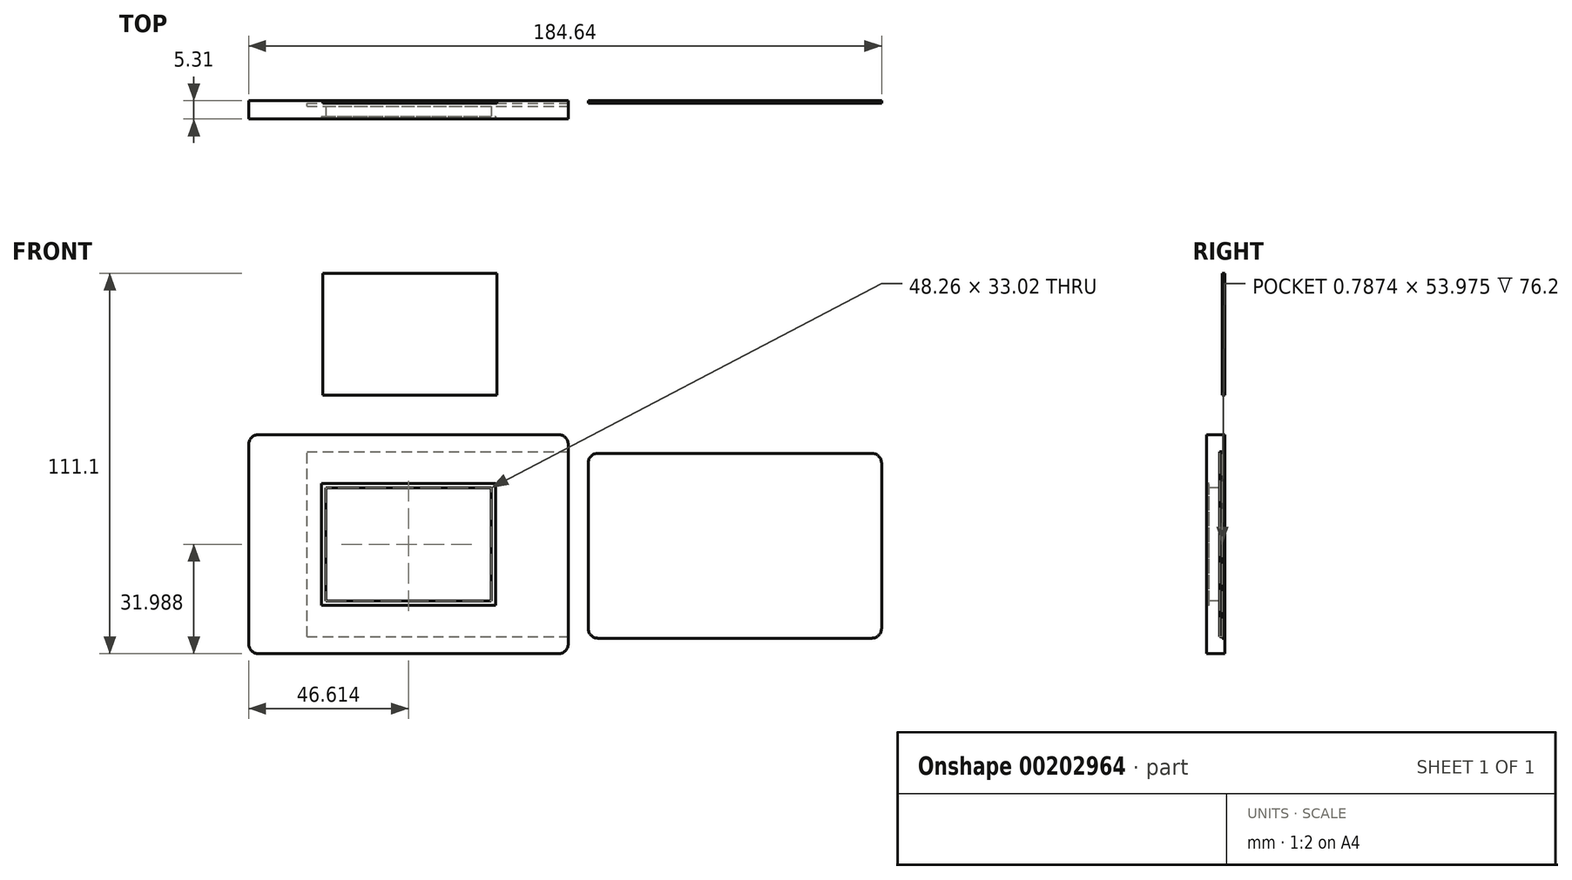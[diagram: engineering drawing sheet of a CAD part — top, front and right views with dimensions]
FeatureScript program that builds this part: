
annotation { "Feature Type Name" : "Feature", "Feature Type Description" : "" }
export const myFeature = defineFeature(function(context is Context, id is Id, definition is map)
    precondition{}
    {
        {
            var Q0;
            Q0=qCreatedBy(makeId("Front.planeOp"),FACE);
            var sketch = newSketch(context, id + "F0", { "sketchPlane" : qUnion([Q0])});
            skLineSegment(sketch, "E0", {"start": v(0, -2.88) * mm, "end": v(0, -51.1) * mm});
            skLineSegment(sketch, "E1", {"start": v(2.88, -53.97) * mm, "end": v(82.72, -53.97) * mm});
            skLineSegment(sketch, "E2", {"start": v(85.6, -51.1) * mm, "end": v(85.6, -2.88) * mm});
            skLineSegment(sketch, "E3", {"start": v(82.72, 0) * mm, "end": v(2.88, 0) * mm});
            skPoint(sketch, "E4.visualSharp", {"position": v(0, 0) * mm});
            skArc(sketch, "E4.filletArc", {"start": v(2.88, 0) * mm, "mid": v(0.84, -0.84) * mm, "end": v(0, -2.88) * mm});
            skPoint(sketch, "E5.visualSharp", {"position": v(85.6, 0) * mm});
            skArc(sketch, "E5.filletArc", {"start": v(85.6, -2.88) * mm, "mid": v(84.75, -0.84) * mm, "end": v(82.72, 0) * mm});
            skPoint(sketch, "E6.visualSharp", {"position": v(85.6, -53.97) * mm});
            skArc(sketch, "E6.filletArc", {"start": v(82.72, -53.98) * mm, "mid": v(84.75, -53.13) * mm, "end": v(85.6, -51.1) * mm});
            skPoint(sketch, "E7.visualSharp", {"position": v(0, -53.97) * mm});
            skArc(sketch, "E7.filletArc", {"start": v(0, -51.1) * mm, "mid": v(0.84, -53.13) * mm, "end": v(2.88, -53.98) * mm});
            skLineSegment(sketch, "E8", {"start": v(-99.04, 2.58) * mm, "end": v(-99.04, -55.64) * mm});
            skLineSegment(sketch, "E9", {"start": v(-96.16, -58.52) * mm, "end": v(-8.7, -58.52) * mm});
            skLineSegment(sketch, "E10", {"start": v(-5.82, -55.64) * mm, "end": v(-5.82, 2.58) * mm});
            skLineSegment(sketch, "E11", {"start": v(-8.7, 5.46) * mm, "end": v(-96.16, 5.46) * mm});
            skPoint(sketch, "E12.visualSharp", {"position": v(-99.04, 5.46) * mm});
            skArc(sketch, "E12.filletArc", {"start": v(-96.16, 5.46) * mm, "mid": v(-98.2, 4.61) * mm, "end": v(-99.04, 2.58) * mm});
            skPoint(sketch, "E13.visualSharp", {"position": v(-5.82, 5.46) * mm});
            skArc(sketch, "E13.filletArc", {"start": v(-5.82, 2.58) * mm, "mid": v(-6.66, 4.61) * mm, "end": v(-8.7, 5.46) * mm});
            skPoint(sketch, "E14.visualSharp", {"position": v(-5.82, -58.52) * mm});
            skArc(sketch, "E14.filletArc", {"start": v(-8.7, -58.52) * mm, "mid": v(-6.66, -57.68) * mm, "end": v(-5.82, -55.64) * mm});
            skPoint(sketch, "E15.visualSharp", {"position": v(-99.04, -58.52) * mm});
            skArc(sketch, "E15.filletArc", {"start": v(-99.04, -55.64) * mm, "mid": v(-98.2, -57.68) * mm, "end": v(-96.16, -58.52) * mm});
            skSolve(sketch);
        }
        {
            var Q0;
            Q0=makeQuery(id+"F0.imprint","IMPRINT",FACE,{"disambiguationData":[TD([[makeQuery(id+"F0.imprint","IMPRINT",EDGE,{"derivedFrom":sQuery(id+"F0.wireOp",EDGE,"E0")}),1.0]])]});
            extrude(context, id + "F1", {"entities" : qUnion([Q0]), "depth" : 0.76 * mm});
        }
        {
            var Q0;
            Q0=makeQuery(id+"F0.imprint","IMPRINT",FACE,{"disambiguationData":[TD([[makeQuery(id+"F0.imprint","IMPRINT",EDGE,{"derivedFrom":sQuery(id+"F0.wireOp",EDGE,"E8")}),1.0]])]});
            extrude(context, id + "F2", {"entities" : qUnion([Q0]), "depth" : 5.3 * mm});
        }
        {
            var Q0;
            Q0=makeQuery(id+"F2.opExtrude","SWEPT_FACE",FACE,{"disambiguationData":[OSD([sQuery(id+"F0.wireOp",EDGE,"E10")])]});
            var sketch = newSketch(context, id + "F3", { "sketchPlane" : qUnion([Q0])});
            skLineSegment(sketch, "E16", {"start": v(0, -26.53) * mm, "end": v(-0.76, -26.53) * mm});
            skPoint(sketch, "E16.endSnap0", {"position": v(0, -26.53) * mm});
            skLineSegment(sketch, "E17", {"start": v(-1.55, -26.53) * mm, "end": v(-1.55, 0.46) * mm});
            skLineSegment(sketch, "E18", {"start": v(-1.55, -26.53) * mm, "end": v(-1.55, -53.52) * mm});
            skLineSegment(sketch, "E19", {"start": v(-0.76, -26.53) * mm, "end": v(-0.76, -53.52) * mm});
            skLineSegment(sketch, "E20", {"start": v(-0.76, -26.53) * mm, "end": v(-0.76, 0.46) * mm});
            skLineSegment(sketch, "E21", {"start": v(-1.55, 0.46) * mm, "end": v(-0.76, 0.46) * mm});
            skLineSegment(sketch, "E22", {"start": v(-1.55, -53.52) * mm, "end": v(-0.76, -53.52) * mm});
            skLineSegment(sketch, "E23", {"start": v(-0.76, -26.53) * mm, "end": v(-1.55, -26.53) * mm});
            skSolve(sketch);
        }
        {
            var Q0;
            Q0=makeQuery(id+"F2.opExtrude","CAP_FACE",FACE,{"disambiguationData":[OSD([sQuery(id+"F0.wireOp",EDGE,"E8"),sQuery(id+"F0.wireOp",EDGE,"E9"),sQuery(id+"F0.wireOp",EDGE,"E10"),sQuery(id+"F0.wireOp",EDGE,"E11"),sQuery(id+"F0.wireOp",EDGE,"E12.filletArc"),sQuery(id+"F0.wireOp",EDGE,"E13.filletArc"),sQuery(id+"F0.wireOp",EDGE,"E14.filletArc"),sQuery(id+"F0.wireOp",EDGE,"E15.filletArc")])],"isStart":false});
            var sketch = newSketch(context, id + "F4", { "sketchPlane" : qUnion([Q0])});
            skPoint(sketch, "E24.orphan", {"position": v(-5.82, -26.53) * mm});
            skPoint(sketch, "E25.orphan", {"position": v(-99.04, -26.53) * mm});
            skPoint(sketch, "E26.orphan", {"position": v(-52.43, -58.52) * mm});
            skPoint(sketch, "E27.orphan", {"position": v(-52.43, 5.46) * mm});
            skPoint(sketch, "E28", {"position": v(-52.43, -26.53) * mm});
            skLineSegment(sketch, "E29", {"start": v(-52.43, -26.53) * mm, "end": v(-52.43, -8.75) * mm});
            skLineSegment(sketch, "E30", {"start": v(-52.43, -26.53) * mm, "end": v(-52.43, -44.31) * mm});
            skLineSegment(sketch, "E31", {"start": v(-52.43, -26.53) * mm, "end": v(-77.83, -26.53) * mm});
            skLineSegment(sketch, "E32", {"start": v(-52.43, -26.53) * mm, "end": v(-27.03, -26.53) * mm});
            skLineSegment(sketch, "E33", {"start": v(-77.83, -26.53) * mm, "end": v(-77.83, -8.75) * mm});
            skLineSegment(sketch, "E34", {"start": v(-52.43, -8.75) * mm, "end": v(-77.83, -8.75) * mm});
            skLineSegment(sketch, "E35", {"start": v(-52.43, -8.75) * mm, "end": v(-27.03, -8.75) * mm});
            skLineSegment(sketch, "E36", {"start": v(-52.43, -44.31) * mm, "end": v(-77.83, -44.31) * mm});
            skLineSegment(sketch, "E37", {"start": v(-52.43, -44.31) * mm, "end": v(-27.03, -44.31) * mm});
            skLineSegment(sketch, "E38", {"start": v(-27.03, -26.53) * mm, "end": v(-27.03, -8.75) * mm});
            skLineSegment(sketch, "E39", {"start": v(-27.03, -26.53) * mm, "end": v(-27.03, -44.31) * mm});
            skLineSegment(sketch, "E40", {"start": v(-77.83, -26.53) * mm, "end": v(-77.83, -44.31) * mm});
            skSolve(sketch);
        }
        {
            var Q0;
            Q0=makeQuery(id+"F4.imprint","IMPRINT",FACE,{"disambiguationData":[TD([[makeQuery(id+"F4.imprint","IMPRINT",EDGE,{"derivedFrom":sQuery(id+"F4.wireOp",EDGE,"E29")}),1.0]])]});
            var Q1;
            Q1=makeQuery(id+"F4.imprint","IMPRINT",FACE,{"disambiguationData":[TD([[makeQuery(id+"F4.imprint","IMPRINT",EDGE,{"derivedFrom":sQuery(id+"F4.wireOp",EDGE,"E29")}),-1.0]])]});
            var Q2;
            Q2=makeQuery(id+"F4.imprint","IMPRINT",FACE,{"disambiguationData":[TD([[makeQuery(id+"F4.imprint","IMPRINT",EDGE,{"derivedFrom":sQuery(id+"F4.wireOp",EDGE,"E30")}),1.0]])]});
            var Q3;
            Q3=makeQuery(id+"F4.imprint","IMPRINT",FACE,{"disambiguationData":[TD([[makeQuery(id+"F4.imprint","IMPRINT",EDGE,{"derivedFrom":sQuery(id+"F4.wireOp",EDGE,"E30")}),-1.0]])]});
            extrude(context, id + "F5", {"entities" : qUnion([Q0, Q1, Q2, Q3]), "operationType" : NewBodyOperationType.REMOVE, "oppositeDirection" : true, "depth" : 0.76 * mm});
        }
        {
            var Q0;
            Q0=makeQuery(id+"F5.boolean.opBoolean","COPY",FACE,{"derivedFrom":makeQuery(id+"F5.opExtrude","CAP_FACE",FACE,{"disambiguationData":[OSD([sQuery(id+"F4.wireOp",EDGE,"E33"),sQuery(id+"F4.wireOp",EDGE,"E34"),sQuery(id+"F4.wireOp",EDGE,"E35"),sQuery(id+"F4.wireOp",EDGE,"E36"),sQuery(id+"F4.wireOp",EDGE,"E37"),sQuery(id+"F4.wireOp",EDGE,"E38"),sQuery(id+"F4.wireOp",EDGE,"E39"),sQuery(id+"F4.wireOp",EDGE,"E40")])],"isStart":false})});
            var sketch = newSketch(context, id + "F6", { "sketchPlane" : qUnion([Q0])});
            skLineSegment(sketch, "E41", {"start": v(-52.43, -8.75) * mm, "end": v(-52.43, -10.02) * mm});
            skLineSegment(sketch, "E42", {"start": v(-77.83, -26.53) * mm, "end": v(-76.56, -26.53) * mm});
            skLineSegment(sketch, "E43", {"start": v(-52.43, -44.31) * mm, "end": v(-52.43, -43.04) * mm});
            skLineSegment(sketch, "E44", {"start": v(-27.03, -26.53) * mm, "end": v(-28.3, -26.53) * mm});
            skLineSegment(sketch, "E45", {"start": v(-52.43, -10.02) * mm, "end": v(-76.56, -10.02) * mm});
            skLineSegment(sketch, "E46", {"start": v(-52.43, -10.02) * mm, "end": v(-28.3, -10.02) * mm});
            skLineSegment(sketch, "E47", {"start": v(-52.43, -43.04) * mm, "end": v(-76.56, -43.04) * mm});
            skLineSegment(sketch, "E48", {"start": v(-52.43, -43.04) * mm, "end": v(-28.3, -43.04) * mm});
            skLineSegment(sketch, "E49", {"start": v(-28.3, -26.53) * mm, "end": v(-28.3, -10.02) * mm});
            skLineSegment(sketch, "E50", {"start": v(-28.3, -26.53) * mm, "end": v(-28.3, -43.04) * mm});
            skLineSegment(sketch, "E51", {"start": v(-76.56, -26.53) * mm, "end": v(-76.56, -10.02) * mm});
            skLineSegment(sketch, "E52", {"start": v(-76.56, -26.53) * mm, "end": v(-76.56, -43.04) * mm});
            skPoint(sketch, "E53.orphan", {"position": v(-27.03, -10.02) * mm});
            skSolve(sketch);
        }
        {
            var Q0;
            Q0=makeQuery(id+"F6.imprint","IMPRINT",FACE,{"disambiguationData":[TD([[makeQuery(id+"F6.imprint","IMPRINT",EDGE,{"derivedFrom":sQuery(id+"F6.wireOp",EDGE,"E45")}),1.0]])]});
            extrude(context, id + "F7", {"entities" : qUnion([Q0]), "operationType" : NewBodyOperationType.REMOVE, "oppositeDirection" : true, "depth" : 3 * mm});
        }
        {
            var Q0;
            Q0=qCreatedBy(makeId("Front.planeOp"),FACE);
            var sketch = newSketch(context, id + "F8", { "sketchPlane" : qUnion([Q0])});
            skLineSegment(sketch, "E54", {"start": v(-77.47, 17.02) * mm, "end": v(-77.47, 52.58) * mm});
            skLineSegment(sketch, "E55", {"start": v(-77.47, 52.58) * mm, "end": v(-26.67, 52.58) * mm});
            skLineSegment(sketch, "E56", {"start": v(-26.67, 52.58) * mm, "end": v(-26.67, 17.02) * mm});
            skLineSegment(sketch, "E57", {"start": v(-77.47, 17.02) * mm, "end": v(-26.67, 17.02) * mm});
            skSolve(sketch);
        }
        {
            var Q0;
            Q0=makeQuery(id+"F8.imprint","IMPRINT",FACE,{"disambiguationData":[TD([[makeQuery(id+"F8.imprint","IMPRINT",EDGE,{"derivedFrom":sQuery(id+"F8.wireOp",EDGE,"E54")}),-1.0]])]});
            extrude(context, id + "F9", {"entities" : qUnion([Q0]), "depth" : 0.76 * mm});
        }
        {
            var Q0;
            Q0=makeQuery(id+"F3.imprint","IMPRINT",FACE,{"disambiguationData":[TD([[makeQuery(id+"F3.imprint","IMPRINT",EDGE,{"derivedFrom":sQuery(id+"F3.wireOp",EDGE,"E17")}),-1.0]])]});
            var Q1;
            Q1=makeQuery(id+"F3.imprint","IMPRINT",FACE,{"disambiguationData":[TD([[makeQuery(id+"F3.imprint","IMPRINT",EDGE,{"derivedFrom":sQuery(id+"F3.wireOp",EDGE,"E18")}),1.0]])]});
            extrude(context, id + "F10", {"entities" : qUnion([Q0, Q1]), "operationType" : NewBodyOperationType.REMOVE, "oppositeDirection" : true, "depth" : 76.2 * mm});
        }
    });
